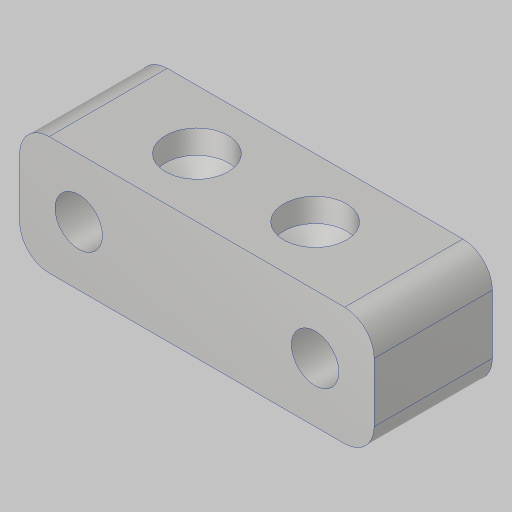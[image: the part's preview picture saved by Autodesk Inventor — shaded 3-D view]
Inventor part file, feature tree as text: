
AUTODESK INVENTOR PART (.ipt)
format: ipt  version: 2023.5 (Build 275446000, 446)  size: 141,824 bytes
history: native  units: in
note: dims shown in document units (in); Inventor stores cm internally (conversion verified against a paired STEP export)
features: sketch x3, hole x2, extrude x1, fillet x1
ambient origin geometry x8: Origin, YZ Plane, XZ Plane, XY Plane, X Axis, Y Axis, Z Axis, Center Point
bodies: Solid1 (feature_tree)
feature tree (7):
  extrude  "Extrusion1"  Depth=0.5in
  sketch  "Sketch2"  dims[d2=0.5in d3=0.0in d4=0.5in]
  hole  "Hole2"  [1 undecoded]
  hole  "Hole3"  [1 undecoded]
  fillet  "Fillet1"  Radius=0.125in
  sketch  "Sketch1"  dims[d0=1.5in d1=0.5in]
  sketch  "Sketch3"  dims[d12=1.0in d13=0.201in d14=0.38in d15=0.375in d16=0.25in d17=0.5635in d18=1.0in d19=0.8108in d20=0.25in d21=0.266in d22=0.75in d23=0.507in d24=0.25in d25=0.5635in d26=0.1in d27=0.8108in d28=0.125in]
note: 2 required parameter values undecoded (feature->parameter linkage not recoverable at this tier; creation-order binding heuristic only, values carry confidence <= 0.55)
